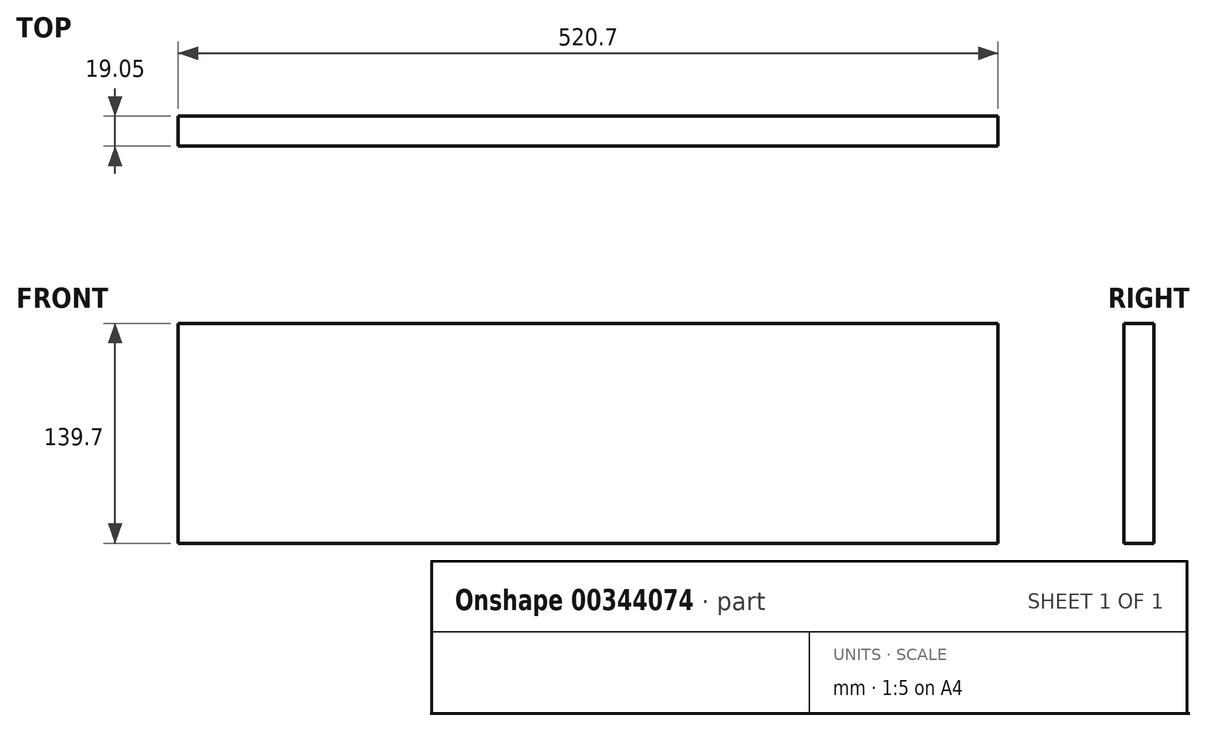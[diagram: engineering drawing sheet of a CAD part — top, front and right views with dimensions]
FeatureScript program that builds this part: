
annotation { "Feature Type Name" : "Feature", "Feature Type Description" : "" }
export const myFeature = defineFeature(function(context is Context, id is Id, definition is map)
    precondition{}
    {
        {
            var Q0;
            Q0=qCreatedBy(makeId("Front.planeOp"),FACE);
            var sketch = newSketch(context, id + "F0", { "sketchPlane" : qUnion([Q0])});
            skLineSegment(sketch, "E0.bottom", {"start": v(0, 0) * mm, "end": v(520.7, 0) * mm});
            skLineSegment(sketch, "E0.top", {"start": v(0, 139.7) * mm, "end": v(520.7, 139.7) * mm});
            skLineSegment(sketch, "E0.left", {"start": v(0, 0) * mm, "end": v(0, 139.7) * mm});
            skLineSegment(sketch, "E0.right", {"start": v(520.7, 0) * mm, "end": v(520.7, 139.7) * mm});
            skSolve(sketch);
        }
        {
            var Q0;
            Q0=qSketchRegion(id+"F0",true);
            extrude(context, id + "F1", {"entities" : qUnion([Q0]), "depth" : 19.05 * mm});
        }
    });
